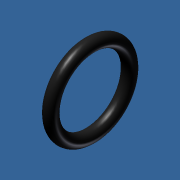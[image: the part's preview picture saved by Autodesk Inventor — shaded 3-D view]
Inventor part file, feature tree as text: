
AUTODESK INVENTOR PART (.ipt)
format: ipt  version: unknown  size: 190,464 bytes
history: native  units: in
note: dims shown in document units (in); Inventor stores cm internally (conversion verified against a paired STEP export)
features: revolve x1, sketch x1
ambient origin geometry x8: Origin, YZ Plane, XZ Plane, XY Plane, X Axis, Y Axis, Z Axis, Center Point
bodies: Solid1 (feature_tree)
feature tree (2):
  revolve  "Revolution1"  [1 undecoded]
  sketch  "Sketch1"  dims[d0=0.125in d1=0.3355in d2=90.0deg]
note: 1 required parameter value undecoded (feature->parameter linkage not recoverable at this tier; creation-order binding heuristic only, values carry confidence <= 0.55)
